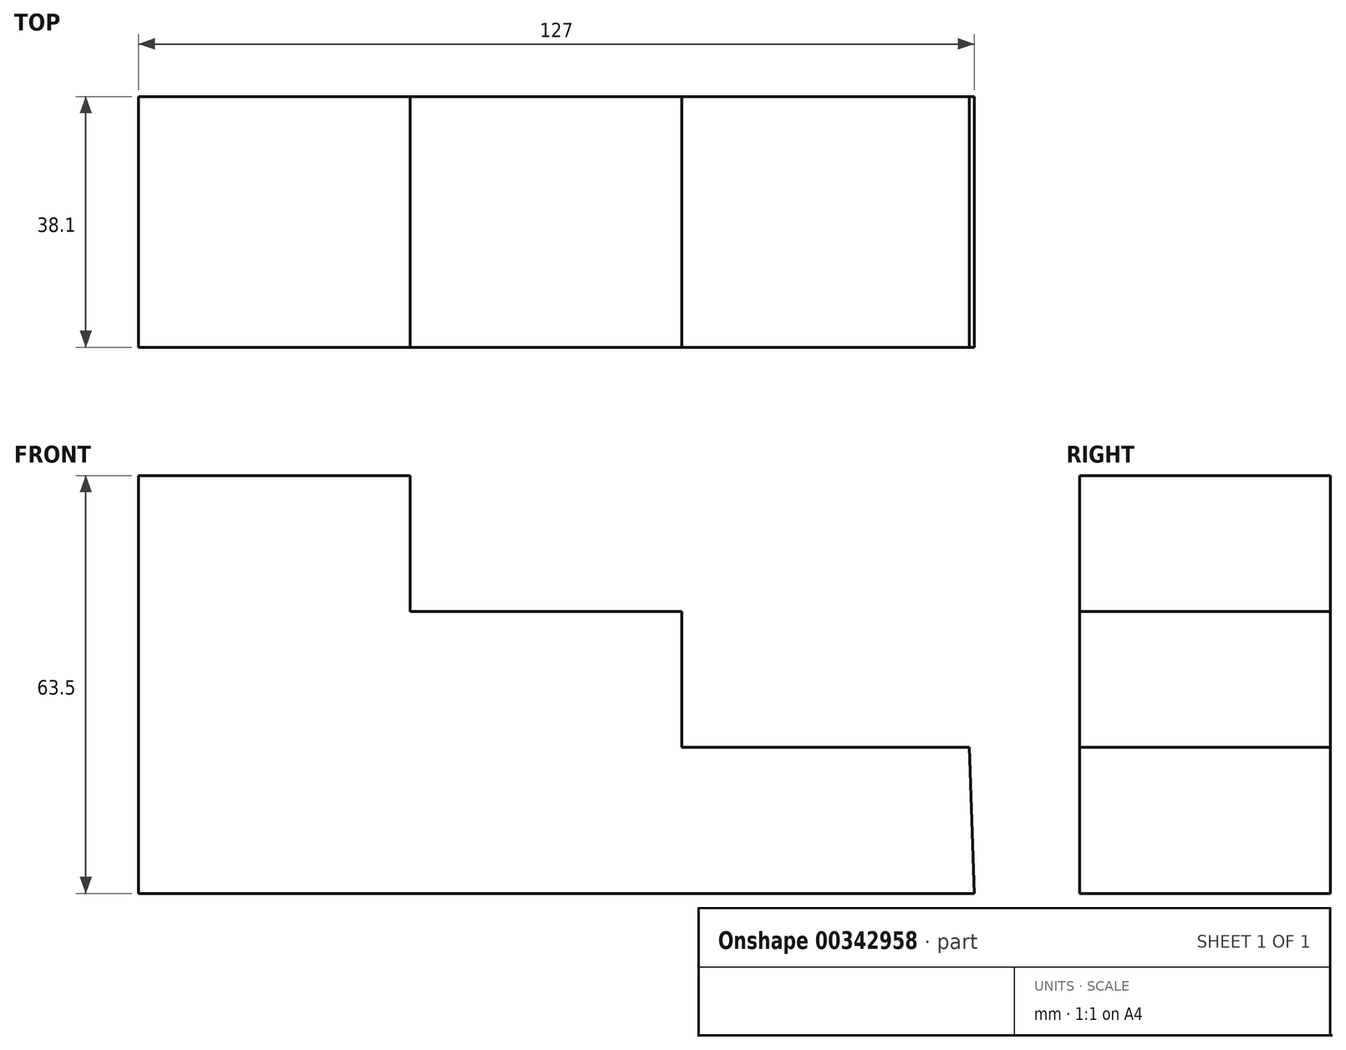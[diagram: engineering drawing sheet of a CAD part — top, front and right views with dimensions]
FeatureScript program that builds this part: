
annotation { "Feature Type Name" : "Feature", "Feature Type Description" : "" }
export const myFeature = defineFeature(function(context is Context, id is Id, definition is map)
    precondition{}
    {
        {
            var Q0;
            Q0=qCreatedBy(makeId("Front.planeOp"),FACE);
            var sketch = newSketch(context, id + "F0", { "sketchPlane" : qUnion([Q0])});
            skLineSegment(sketch, "E0", {"start": v(-34.98, 22.71) * mm, "end": v(-34.98, -40.79) * mm});
            skLineSegment(sketch, "E1", {"start": v(-34.98, -40.79) * mm, "end": v(92.02, -40.79) * mm});
            skLineSegment(sketch, "E2", {"start": v(-34.98, 22.71) * mm, "end": v(6.3, 22.71) * mm});
            skLineSegment(sketch, "E3", {"start": v(6.3, 22.71) * mm, "end": v(6.3, 2.06) * mm});
            skLineSegment(sketch, "E4", {"start": v(6.3, 2.06) * mm, "end": v(47.57, 2.06) * mm});
            skLineSegment(sketch, "E5", {"start": v(47.57, 2.06) * mm, "end": v(47.57, -18.59) * mm});
            skLineSegment(sketch, "E6", {"start": v(47.57, -18.59) * mm, "end": v(91.23, -18.59) * mm});
            skLineSegment(sketch, "E7", {"start": v(91.23, -18.59) * mm, "end": v(92.02, -40.79) * mm});
            skSolve(sketch);
        }
        {
            var Q0;
            Q0 = qSketchRegion(id + "F0", true);
            extrude(context, id + "F1", {"entities" : qUnion([Q0]), "depth" : 38.1 * mm});
        }
    });
